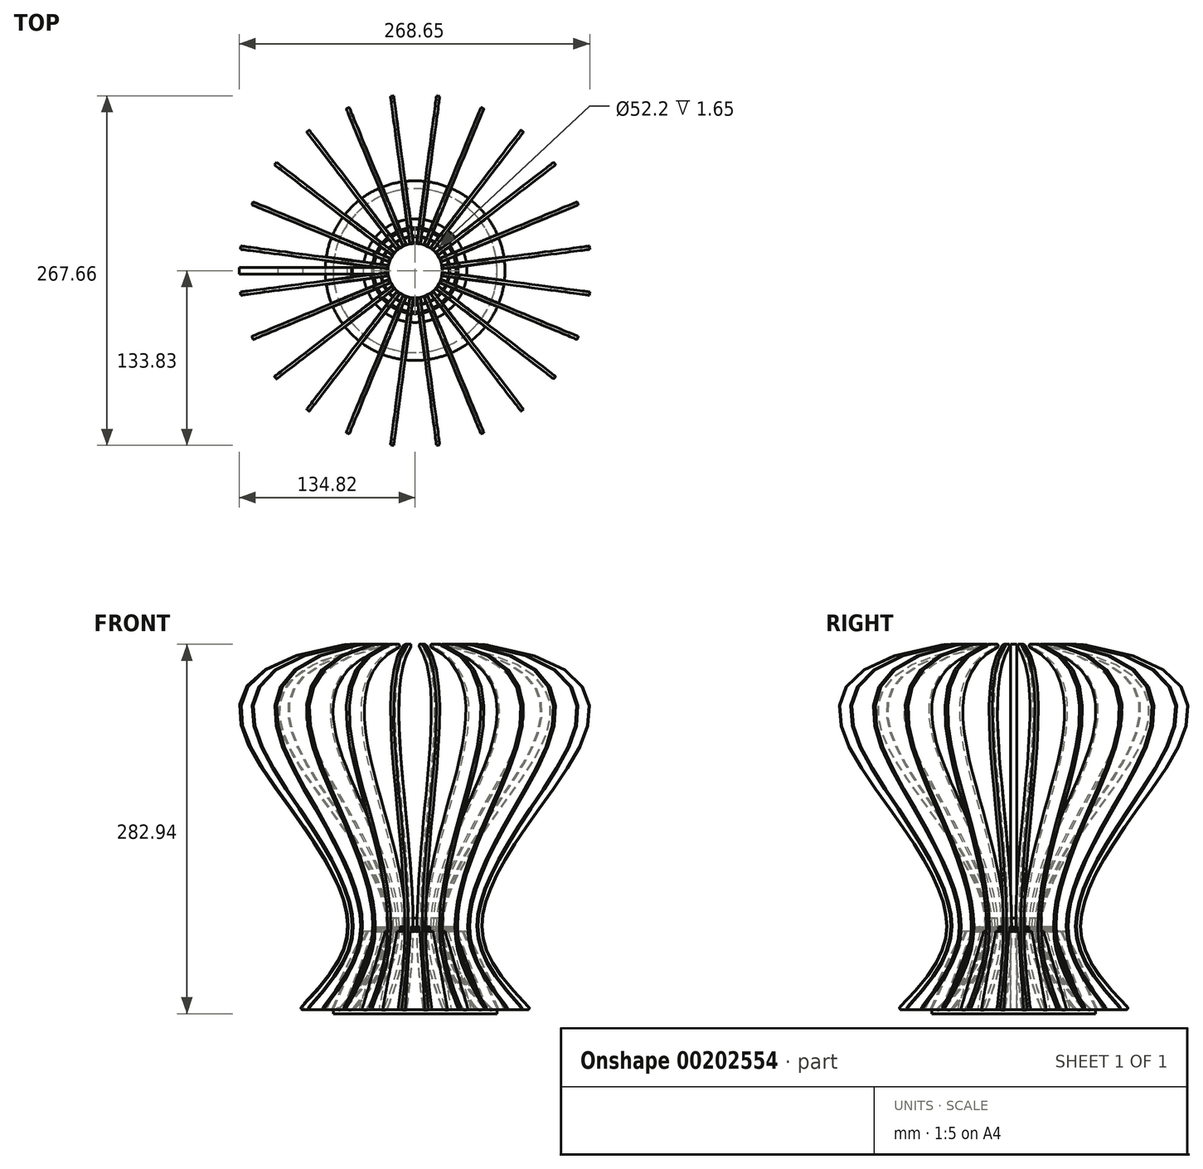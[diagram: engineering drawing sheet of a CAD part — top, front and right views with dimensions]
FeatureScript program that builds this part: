
annotation { "Feature Type Name" : "Feature", "Feature Type Description" : "" }
export const myFeature = defineFeature(function(context is Context, id is Id, definition is map)
    precondition{}
    {
        {
            var Q0;
            Q0=qCreatedBy(makeId("Top.planeOp"),FACE);
            var sketch = newSketch(context, id + "F0", { "sketchPlane" : qUnion([Q0])});
            skCircle(sketch, "E0", {"center": v(0, 0) * mm, "radius": 32.75 * mm});
            skCircle(sketch, "E1", {"center": v(0, 0) * mm, "radius": 26.1 * mm});
            skSolve(sketch);
        }
        {
            var Q0;
            Q0=qSketchRegion(id+"F0",true);
            extrude(context, id + "F1", {"entities" : qUnion([Q0]), "depth" : 1.65 * mm});
        }
        {
            var Q0;
            Q0=makeQuery(id+"F1.opExtrude","CAP_FACE",FACE,{"disambiguationData":[OSD([sQuery(id+"F0.wireOp",EDGE,"E0"),sQuery(id+"F0.wireOp",EDGE,"E1")])],"isStart":false});
            var sketch = newSketch(context, id + "F2", { "sketchPlane" : qUnion([Q0])});
            skLineSegment(sketch, "E2.bottom", {"start": v(2.5, -26.5) * mm, "end": v(-2.5, -26.5) * mm});
            skLineSegment(sketch, "E2.top", {"start": v(2.5, -31.5) * mm, "end": v(-2.5, -31.5) * mm});
            skLineSegment(sketch, "E2.left", {"start": v(2.5, -26.5) * mm, "end": v(2.5, -31.5) * mm});
            skLineSegment(sketch, "E2.right", {"start": v(-2.5, -26.5) * mm, "end": v(-2.5, -31.5) * mm});
            skPoint(sketch, "E2.middle", {"position": v(0, -29) * mm});
            skSolve(sketch);
        }
        {
            var Q0;
            Q0=makeQuery(id+"F2.imprint","IMPRINT",FACE,{"disambiguationData":[TD([[makeQuery(id+"F2.imprint","IMPRINT",EDGE,{"derivedFrom":sQuery(id+"F2.wireOp",EDGE,"E2.bottom")}),1.0]])]});
            extrude(context, id + "F3", {"entities" : qUnion([Q0]), "depth" : 1.62 * mm});
        }
        {
            var Q0;
            Q0=makeQuery(id+"F3.opExtrude","SWEPT_BODY",BODY,{"disambiguationData":[OSD([sQuery(id+"F2.wireOp",EDGE,"E2.bottom"),sQuery(id+"F2.wireOp",EDGE,"E2.top"),sQuery(id+"F2.wireOp",EDGE,"E2.left"),sQuery(id+"F2.wireOp",EDGE,"E2.right")])]});
            var Q1;
            Q1=makeQuery(id+"F1.opExtrude","CAP_EDGE",EDGE,{"disambiguationData":[OSD([sQuery(id+"F0.wireOp",EDGE,"E0")])],"isStart":false});
            circularPattern(context, id + "F4", {"entities" : qUnion([Q0]), "axis" : qUnion([Q1]), "angle" : 360 * degree, "instanceCount" : 24, "equalSpace" : true});
        }
        {
            var Q0;
            Q0=qCreatedBy(makeId("Front.planeOp"),FACE);
            var sketch = newSketch(context, id + "F5", { "sketchPlane" : qUnion([Q0])});
            skFitSpline(sketch, "E3", {"points": [v(-52, 220) * mm, v(-100, 100) * mm, v(-52, 10) * mm, v(-90, -60) * mm], "startDerivative": vector(-1003.67, -146.83) * mm, "endDerivative": vector(-314.48, -306.5) * mm});
            skLineSegment(sketch, "E4", {"start": v(-9.97, -59.99) * mm, "end": v(-9.97, -0.01) * mm, "construction": true});
            skLineSegment(sketch, "E5", {"start": v(-9.97, -0.01) * mm, "end": v(-33, -0.01) * mm});
            skLineSegment(sketch, "E6", {"start": v(-33, -0.01) * mm, "end": v(-33, 3.46) * mm});
            skLineSegment(sketch, "E7", {"start": v(-33, 3.46) * mm, "end": v(0, 3.46) * mm});
            skLineSegment(sketch, "E8", {"start": v(0, 3.46) * mm, "end": v(0, 369.62) * mm, "construction": true});
            skLineSegment(sketch, "E9", {"start": v(-22, 3.46) * mm, "end": v(-22, 220) * mm, "construction": true});
            skFitSpline(sketch, "E10", {"points": [v(-60, -60) * mm, v(-22, 10) * mm, v(-70, 100) * mm, v(-22, 220) * mm], "startDerivative": vector(314.48, 306.5) * mm, "endDerivative": vector(1003.67, 146.83) * mm});
            skLineSegment(sketch, "E11", {"start": v(-90, -60) * mm, "end": v(-60, -60) * mm});
            skLineSegment(sketch, "E12", {"start": v(-59.22, -30) * mm, "end": v(-29.22, -30) * mm, "construction": true});
            skLineSegment(sketch, "E13", {"start": v(-52, 10) * mm, "end": v(-22, 10) * mm, "construction": true});
            skLineSegment(sketch, "E14", {"start": v(-52, 220) * mm, "end": v(-22, 220) * mm});
            skLineSegment(sketch, "E15", {"start": v(-177.14, 201.7) * mm, "end": v(-147.14, 201.7) * mm, "construction": true});
            skLineSegment(sketch, "E16", {"start": v(-100, 100) * mm, "end": v(-70, 100) * mm, "construction": true});
            skPoint(sketch, "E17", {"position": v(-9.97, -30) * mm});
            skSolve(sketch);
        }
        {
            var Q0;
            Q0=makeQuery(id+"F5.imprint","IMPRINT",FACE,{"disambiguationData":[TD([[makeQuery(id+"F5.imprint","IMPRINT",EDGE,{"derivedFrom":sQuery(id+"F5.wireOp",EDGE,"E3")}),1.0]])]});
            extrude(context, id + "F6", {"entities" : qUnion([Q0]), "endBound" : BoundingType.SYMMETRIC, "depth" : 5 * mm});
        }
        {
            var Q0;
            Q0=makeQuery(id+"F6.opExtrude","SWEPT_EDGE",EDGE,{"disambiguationData":[OSD([sQuery(id+"F5.wireOp",EDGE,"E3"),sQuery(id+"F5.wireOp",EDGE,"E14")])]});
            fillet(context, id + "F7", {"entities" : qUnion([Q0]), "radius" : 46.48 * mm, "tangentPropagation" : true, "allowEdgeOverflow" : false});
        }
        {
            var Q0;
            Q0=makeQuery(id+"F6.opExtrude","SWEPT_EDGE",EDGE,{"disambiguationData":[OSD([sQuery(id+"F5.wireOp",EDGE,"E10"),sQuery(id+"F5.wireOp",EDGE,"E14")])]});
            fillet(context, id + "F8", {"entities" : qUnion([Q0]), "radius" : 3.7 * mm, "tangentPropagation" : true, "allowEdgeOverflow" : false});
        }
        {
            var Q0;
            Q0=makeQuery(id+"F6.opExtrude","SWEPT_EDGE",EDGE,{"disambiguationData":[OSD([sQuery(id+"F5.wireOp",EDGE,"E3"),sQuery(id+"F5.wireOp",EDGE,"E11")])]});
            fillet(context, id + "F9", {"entities" : qUnion([Q0]), "radius" : 2.86 * mm, "tangentPropagation" : true, "allowEdgeOverflow" : false});
        }
        {
            var Q0;
            Q0=makeQuery(id+"F6.opExtrude","SWEPT_EDGE",EDGE,{"disambiguationData":[OSD([sQuery(id+"F5.wireOp",EDGE,"E10"),sQuery(id+"F5.wireOp",EDGE,"E11")])]});
            fillet(context, id + "F10", {"entities" : qUnion([Q0]), "radius" : 13.3 * mm, "tangentPropagation" : true, "allowEdgeOverflow" : false});
        }
        {
            var Q0;
            Q0=makeQuery(id+"F5.imprint","IMPRINT",FACE,{"disambiguationData":[TD([[makeQuery(id+"F5.imprint","IMPRINT",EDGE,{"derivedFrom":sQuery(id+"F5.wireOp",EDGE,"E3")}),1.0]])]});
            extrude(context, id + "F11", {"entities" : qUnion([Q0]), "endBound" : BoundingType.SYMMETRIC, "depth" : 2.5 * mm});
        }
        {
            var Q0;
            Q0=makeQuery(id+"F11.opExtrude","SWEPT_EDGE",EDGE,{"disambiguationData":[OSD([sQuery(id+"F5.wireOp",EDGE,"E3"),sQuery(id+"F5.wireOp",EDGE,"E14")])]});
            fillet(context, id + "F12", {"entities" : qUnion([Q0]), "radius" : 59.56 * mm, "tangentPropagation" : true, "allowEdgeOverflow" : false});
        }
        {
            var Q0;
            Q0=makeQuery(id+"F11.opExtrude","SWEPT_EDGE",EDGE,{"disambiguationData":[OSD([sQuery(id+"F5.wireOp",EDGE,"E10"),sQuery(id+"F5.wireOp",EDGE,"E14")])]});
            fillet(context, id + "F13", {"entities" : qUnion([Q0]), "radius" : 1.1 * mm, "tangentPropagation" : true, "allowEdgeOverflow" : false});
        }
        {
            var Q0;
            Q0=makeQuery(id+"F11.opExtrude","SWEPT_EDGE",EDGE,{"disambiguationData":[OSD([sQuery(id+"F5.wireOp",EDGE,"E3"),sQuery(id+"F5.wireOp",EDGE,"E11")])]});
            fillet(context, id + "F14", {"entities" : qUnion([Q0]), "radius" : 1.37 * mm, "tangentPropagation" : true, "allowEdgeOverflow" : false});
        }
        {
            var Q0;
            Q0=makeQuery(id+"F11.opExtrude","SWEPT_EDGE",EDGE,{"disambiguationData":[OSD([sQuery(id+"F5.wireOp",EDGE,"E10"),sQuery(id+"F5.wireOp",EDGE,"E11")])]});
            fillet(context, id + "F15", {"entities" : qUnion([Q0]), "radius" : 6.04 * mm, "tangentPropagation" : true, "allowEdgeOverflow" : false});
        }
        {
            var Q0;
            Q0=makeQuery(id+"F11.opExtrude","SWEPT_BODY",BODY,{"disambiguationData":[OSD([sQuery(id+"F5.wireOp",EDGE,"E3"),sQuery(id+"F5.wireOp",EDGE,"E5"),sQuery(id+"F5.wireOp",EDGE,"E6"),sQuery(id+"F5.wireOp",EDGE,"E7"),sQuery(id+"F5.wireOp",EDGE,"E10"),sQuery(id+"F5.wireOp",EDGE,"E11"),sQuery(id+"F5.wireOp",EDGE,"E14")])]});
            var Q1;
            Q1=sQuery(id+"F5.wireOp",EDGE,"E8");
            transform(context, id + "F16", {"entities" : qUnion([Q0]), "transformType" : TransformType.ROTATION, "transformAxis" : qUnion([Q1]), "angle" : 7.5 * degree, "makeCopy" : false});
        }
        {
            var Q0;
            Q0=makeQuery(id+"F11.opExtrude","SWEPT_BODY",BODY,{"disambiguationData":[OSD([sQuery(id+"F5.wireOp",EDGE,"E3"),sQuery(id+"F5.wireOp",EDGE,"E5"),sQuery(id+"F5.wireOp",EDGE,"E6"),sQuery(id+"F5.wireOp",EDGE,"E7"),sQuery(id+"F5.wireOp",EDGE,"E10"),sQuery(id+"F5.wireOp",EDGE,"E11"),sQuery(id+"F5.wireOp",EDGE,"E14")])]});
            var Q1;
            Q1=sQuery(id+"F5.wireOp",EDGE,"E8");
            circularPattern(context, id + "F17", {"entities" : qUnion([Q0]), "axis" : qUnion([Q1]), "angle" : 360 * degree, "instanceCount" : 24, "equalSpace" : true});
        }
        {
            var Q0;
            Q0=qCreatedBy(makeId("Front.planeOp"),FACE);
            var sketch = newSketch(context, id + "F18", { "sketchPlane" : qUnion([Q0])});
            skLineSegment(sketch, "E18", {"start": v(0, -59.93) * mm, "end": v(-68.82, -59.93) * mm});
            skLineSegment(sketch, "E19", {"start": v(-68.82, -59.93) * mm, "end": v(-39.68, 0) * mm});
            skLineSegment(sketch, "E20", {"start": v(-39.68, 0) * mm, "end": v(-20.78, 0) * mm});
            skLineSegment(sketch, "E21", {"start": v(-20.78, 0) * mm, "end": v(-20.78, 10.18) * mm});
            skLineSegment(sketch, "E22", {"start": v(-20.78, 10.18) * mm, "end": v(0, 10.18) * mm});
            skLineSegment(sketch, "E23", {"start": v(0, 10.18) * mm, "end": v(0, -59.93) * mm});
            skLineSegment(sketch, "E24", {"start": v(-62.79, -59.93) * mm, "end": v(-62.79, -62.94) * mm});
            skLineSegment(sketch, "E25", {"start": v(-62.79, -62.94) * mm, "end": v(0, -62.94) * mm});
            skLineSegment(sketch, "E26", {"start": v(0, -62.94) * mm, "end": v(0, -59.93) * mm});
            skSolve(sketch);
        }
        {
            var Q0;
            {var subQ0=sQuery(id+"F18.wireOp",EDGE,"E19");Q0=makeQuery(id+"F18.imprint","IMPRINT",FACE,{"disambiguationData":[TD([[makeQuery(id+"F18.imprint","IMPRINT",EDGE,{"derivedFrom":subQ0}),-1.0]])]});}
            var Q1;
            {var subQ2=sQuery(id+"F18.wireOp",EDGE,"E24");Q1=makeQuery(id+"F18.imprint","IMPRINT",FACE,{"disambiguationData":[TD([[makeQuery(id+"F18.imprint","IMPRINT",EDGE,{"derivedFrom":subQ2}),1.0]])]});}
            var Q2;
            Q2=sQuery(id+"F18.wireOp",EDGE,"E23");
            revolve(context, id + "F19", {"entities" : qUnion([Q0, Q1]), "axis" : qUnion([Q2]), "revolveType" : RevolveType.FULL});
        }
        {
            var Q0;
            Q0=makeQuery(id+"F17.opPattern","COPY",BODY,{"derivedFrom":makeQuery(id+"F11.opExtrude","SWEPT_BODY",BODY,{"disambiguationData":[OSD([sQuery(id+"F5.wireOp",EDGE,"E3"),sQuery(id+"F5.wireOp",EDGE,"E5"),sQuery(id+"F5.wireOp",EDGE,"E6"),sQuery(id+"F5.wireOp",EDGE,"E7"),sQuery(id+"F5.wireOp",EDGE,"E10"),sQuery(id+"F5.wireOp",EDGE,"E11"),sQuery(id+"F5.wireOp",EDGE,"E14")])]}),"instanceName":"3"});
            var Q1;
            Q1=makeQuery(id+"F17.opPattern","COPY",BODY,{"derivedFrom":makeQuery(id+"F11.opExtrude","SWEPT_BODY",BODY,{"disambiguationData":[OSD([sQuery(id+"F5.wireOp",EDGE,"E3"),sQuery(id+"F5.wireOp",EDGE,"E5"),sQuery(id+"F5.wireOp",EDGE,"E6"),sQuery(id+"F5.wireOp",EDGE,"E7"),sQuery(id+"F5.wireOp",EDGE,"E10"),sQuery(id+"F5.wireOp",EDGE,"E11"),sQuery(id+"F5.wireOp",EDGE,"E14")])]}),"instanceName":"4"});
            var Q2;
            Q2=makeQuery(id+"F17.opPattern","COPY",BODY,{"derivedFrom":makeQuery(id+"F11.opExtrude","SWEPT_BODY",BODY,{"disambiguationData":[OSD([sQuery(id+"F5.wireOp",EDGE,"E3"),sQuery(id+"F5.wireOp",EDGE,"E5"),sQuery(id+"F5.wireOp",EDGE,"E6"),sQuery(id+"F5.wireOp",EDGE,"E7"),sQuery(id+"F5.wireOp",EDGE,"E10"),sQuery(id+"F5.wireOp",EDGE,"E11"),sQuery(id+"F5.wireOp",EDGE,"E14")])]}),"instanceName":"5"});
            var Q3;
            Q3=makeQuery(id+"F17.opPattern","COPY",BODY,{"derivedFrom":makeQuery(id+"F11.opExtrude","SWEPT_BODY",BODY,{"disambiguationData":[OSD([sQuery(id+"F5.wireOp",EDGE,"E3"),sQuery(id+"F5.wireOp",EDGE,"E5"),sQuery(id+"F5.wireOp",EDGE,"E6"),sQuery(id+"F5.wireOp",EDGE,"E7"),sQuery(id+"F5.wireOp",EDGE,"E10"),sQuery(id+"F5.wireOp",EDGE,"E11"),sQuery(id+"F5.wireOp",EDGE,"E14")])]}),"instanceName":"6"});
            var Q4;
            Q4=makeQuery(id+"F17.opPattern","COPY",BODY,{"derivedFrom":makeQuery(id+"F11.opExtrude","SWEPT_BODY",BODY,{"disambiguationData":[OSD([sQuery(id+"F5.wireOp",EDGE,"E3"),sQuery(id+"F5.wireOp",EDGE,"E5"),sQuery(id+"F5.wireOp",EDGE,"E6"),sQuery(id+"F5.wireOp",EDGE,"E7"),sQuery(id+"F5.wireOp",EDGE,"E10"),sQuery(id+"F5.wireOp",EDGE,"E11"),sQuery(id+"F5.wireOp",EDGE,"E14")])]}),"instanceName":"7"});
            var Q5;
            Q5=makeQuery(id+"F17.opPattern","COPY",BODY,{"derivedFrom":makeQuery(id+"F11.opExtrude","SWEPT_BODY",BODY,{"disambiguationData":[OSD([sQuery(id+"F5.wireOp",EDGE,"E3"),sQuery(id+"F5.wireOp",EDGE,"E5"),sQuery(id+"F5.wireOp",EDGE,"E6"),sQuery(id+"F5.wireOp",EDGE,"E7"),sQuery(id+"F5.wireOp",EDGE,"E10"),sQuery(id+"F5.wireOp",EDGE,"E11"),sQuery(id+"F5.wireOp",EDGE,"E14")])]}),"instanceName":"8"});
            var Q6;
            Q6=makeQuery(id+"F17.opPattern","COPY",BODY,{"derivedFrom":makeQuery(id+"F11.opExtrude","SWEPT_BODY",BODY,{"disambiguationData":[OSD([sQuery(id+"F5.wireOp",EDGE,"E3"),sQuery(id+"F5.wireOp",EDGE,"E5"),sQuery(id+"F5.wireOp",EDGE,"E6"),sQuery(id+"F5.wireOp",EDGE,"E7"),sQuery(id+"F5.wireOp",EDGE,"E10"),sQuery(id+"F5.wireOp",EDGE,"E11"),sQuery(id+"F5.wireOp",EDGE,"E14")])]}),"instanceName":"9"});
            var Q7;
            Q7=makeQuery(id+"F17.opPattern","COPY",BODY,{"derivedFrom":makeQuery(id+"F11.opExtrude","SWEPT_BODY",BODY,{"disambiguationData":[OSD([sQuery(id+"F5.wireOp",EDGE,"E3"),sQuery(id+"F5.wireOp",EDGE,"E5"),sQuery(id+"F5.wireOp",EDGE,"E6"),sQuery(id+"F5.wireOp",EDGE,"E7"),sQuery(id+"F5.wireOp",EDGE,"E10"),sQuery(id+"F5.wireOp",EDGE,"E11"),sQuery(id+"F5.wireOp",EDGE,"E14")])]}),"instanceName":"10"});
            var Q8;
            Q8=makeQuery(id+"F17.opPattern","COPY",BODY,{"derivedFrom":makeQuery(id+"F11.opExtrude","SWEPT_BODY",BODY,{"disambiguationData":[OSD([sQuery(id+"F5.wireOp",EDGE,"E3"),sQuery(id+"F5.wireOp",EDGE,"E5"),sQuery(id+"F5.wireOp",EDGE,"E6"),sQuery(id+"F5.wireOp",EDGE,"E7"),sQuery(id+"F5.wireOp",EDGE,"E10"),sQuery(id+"F5.wireOp",EDGE,"E11"),sQuery(id+"F5.wireOp",EDGE,"E14")])]}),"instanceName":"11"});
            var Q9;
            Q9=makeQuery(id+"F17.opPattern","COPY",BODY,{"derivedFrom":makeQuery(id+"F11.opExtrude","SWEPT_BODY",BODY,{"disambiguationData":[OSD([sQuery(id+"F5.wireOp",EDGE,"E3"),sQuery(id+"F5.wireOp",EDGE,"E5"),sQuery(id+"F5.wireOp",EDGE,"E6"),sQuery(id+"F5.wireOp",EDGE,"E7"),sQuery(id+"F5.wireOp",EDGE,"E10"),sQuery(id+"F5.wireOp",EDGE,"E11"),sQuery(id+"F5.wireOp",EDGE,"E14")])]}),"instanceName":"12"});
            var Q10;
            Q10=makeQuery(id+"F17.opPattern","COPY",BODY,{"derivedFrom":makeQuery(id+"F11.opExtrude","SWEPT_BODY",BODY,{"disambiguationData":[OSD([sQuery(id+"F5.wireOp",EDGE,"E3"),sQuery(id+"F5.wireOp",EDGE,"E5"),sQuery(id+"F5.wireOp",EDGE,"E6"),sQuery(id+"F5.wireOp",EDGE,"E7"),sQuery(id+"F5.wireOp",EDGE,"E10"),sQuery(id+"F5.wireOp",EDGE,"E11"),sQuery(id+"F5.wireOp",EDGE,"E14")])]}),"instanceName":"13"});
            var Q11;
            Q11=makeQuery(id+"F17.opPattern","COPY",BODY,{"derivedFrom":makeQuery(id+"F11.opExtrude","SWEPT_BODY",BODY,{"disambiguationData":[OSD([sQuery(id+"F5.wireOp",EDGE,"E3"),sQuery(id+"F5.wireOp",EDGE,"E5"),sQuery(id+"F5.wireOp",EDGE,"E6"),sQuery(id+"F5.wireOp",EDGE,"E7"),sQuery(id+"F5.wireOp",EDGE,"E10"),sQuery(id+"F5.wireOp",EDGE,"E11"),sQuery(id+"F5.wireOp",EDGE,"E14")])]}),"instanceName":"14"});
            var Q12;
            Q12=makeQuery(id+"F17.opPattern","COPY",BODY,{"derivedFrom":makeQuery(id+"F11.opExtrude","SWEPT_BODY",BODY,{"disambiguationData":[OSD([sQuery(id+"F5.wireOp",EDGE,"E3"),sQuery(id+"F5.wireOp",EDGE,"E5"),sQuery(id+"F5.wireOp",EDGE,"E6"),sQuery(id+"F5.wireOp",EDGE,"E7"),sQuery(id+"F5.wireOp",EDGE,"E10"),sQuery(id+"F5.wireOp",EDGE,"E11"),sQuery(id+"F5.wireOp",EDGE,"E14")])]}),"instanceName":"15"});
            var Q13;
            Q13=makeQuery(id+"F17.opPattern","COPY",BODY,{"derivedFrom":makeQuery(id+"F11.opExtrude","SWEPT_BODY",BODY,{"disambiguationData":[OSD([sQuery(id+"F5.wireOp",EDGE,"E3"),sQuery(id+"F5.wireOp",EDGE,"E5"),sQuery(id+"F5.wireOp",EDGE,"E6"),sQuery(id+"F5.wireOp",EDGE,"E7"),sQuery(id+"F5.wireOp",EDGE,"E10"),sQuery(id+"F5.wireOp",EDGE,"E11"),sQuery(id+"F5.wireOp",EDGE,"E14")])]}),"instanceName":"16"});
            var Q14;
            Q14=makeQuery(id+"F17.opPattern","COPY",BODY,{"derivedFrom":makeQuery(id+"F11.opExtrude","SWEPT_BODY",BODY,{"disambiguationData":[OSD([sQuery(id+"F5.wireOp",EDGE,"E3"),sQuery(id+"F5.wireOp",EDGE,"E5"),sQuery(id+"F5.wireOp",EDGE,"E6"),sQuery(id+"F5.wireOp",EDGE,"E7"),sQuery(id+"F5.wireOp",EDGE,"E10"),sQuery(id+"F5.wireOp",EDGE,"E11"),sQuery(id+"F5.wireOp",EDGE,"E14")])]}),"instanceName":"17"});
            var Q15;
            Q15=makeQuery(id+"F17.opPattern","COPY",BODY,{"derivedFrom":makeQuery(id+"F11.opExtrude","SWEPT_BODY",BODY,{"disambiguationData":[OSD([sQuery(id+"F5.wireOp",EDGE,"E3"),sQuery(id+"F5.wireOp",EDGE,"E5"),sQuery(id+"F5.wireOp",EDGE,"E6"),sQuery(id+"F5.wireOp",EDGE,"E7"),sQuery(id+"F5.wireOp",EDGE,"E10"),sQuery(id+"F5.wireOp",EDGE,"E11"),sQuery(id+"F5.wireOp",EDGE,"E14")])]}),"instanceName":"18"});
            var Q16;
            Q16=makeQuery(id+"F17.opPattern","COPY",BODY,{"derivedFrom":makeQuery(id+"F11.opExtrude","SWEPT_BODY",BODY,{"disambiguationData":[OSD([sQuery(id+"F5.wireOp",EDGE,"E3"),sQuery(id+"F5.wireOp",EDGE,"E5"),sQuery(id+"F5.wireOp",EDGE,"E6"),sQuery(id+"F5.wireOp",EDGE,"E7"),sQuery(id+"F5.wireOp",EDGE,"E10"),sQuery(id+"F5.wireOp",EDGE,"E11"),sQuery(id+"F5.wireOp",EDGE,"E14")])]}),"instanceName":"20"});
            var Q17;
            Q17=makeQuery(id+"F17.opPattern","COPY",BODY,{"derivedFrom":makeQuery(id+"F11.opExtrude","SWEPT_BODY",BODY,{"disambiguationData":[OSD([sQuery(id+"F5.wireOp",EDGE,"E3"),sQuery(id+"F5.wireOp",EDGE,"E5"),sQuery(id+"F5.wireOp",EDGE,"E6"),sQuery(id+"F5.wireOp",EDGE,"E7"),sQuery(id+"F5.wireOp",EDGE,"E10"),sQuery(id+"F5.wireOp",EDGE,"E11"),sQuery(id+"F5.wireOp",EDGE,"E14")])]}),"instanceName":"21"});
            var Q18;
            Q18=makeQuery(id+"F17.opPattern","COPY",BODY,{"derivedFrom":makeQuery(id+"F11.opExtrude","SWEPT_BODY",BODY,{"disambiguationData":[OSD([sQuery(id+"F5.wireOp",EDGE,"E3"),sQuery(id+"F5.wireOp",EDGE,"E5"),sQuery(id+"F5.wireOp",EDGE,"E6"),sQuery(id+"F5.wireOp",EDGE,"E7"),sQuery(id+"F5.wireOp",EDGE,"E10"),sQuery(id+"F5.wireOp",EDGE,"E11"),sQuery(id+"F5.wireOp",EDGE,"E14")])]}),"instanceName":"22"});
            var Q19;
            Q19=makeQuery(id+"F17.opPattern","COPY",BODY,{"derivedFrom":makeQuery(id+"F11.opExtrude","SWEPT_BODY",BODY,{"disambiguationData":[OSD([sQuery(id+"F5.wireOp",EDGE,"E3"),sQuery(id+"F5.wireOp",EDGE,"E5"),sQuery(id+"F5.wireOp",EDGE,"E6"),sQuery(id+"F5.wireOp",EDGE,"E7"),sQuery(id+"F5.wireOp",EDGE,"E10"),sQuery(id+"F5.wireOp",EDGE,"E11"),sQuery(id+"F5.wireOp",EDGE,"E14")])]}),"instanceName":"1"});
            var Q20;
            Q20=makeQuery(id+"F11.opExtrude","SWEPT_BODY",BODY,{"disambiguationData":[OSD([sQuery(id+"F5.wireOp",EDGE,"E3"),sQuery(id+"F5.wireOp",EDGE,"E5"),sQuery(id+"F5.wireOp",EDGE,"E6"),sQuery(id+"F5.wireOp",EDGE,"E7"),sQuery(id+"F5.wireOp",EDGE,"E10"),sQuery(id+"F5.wireOp",EDGE,"E11"),sQuery(id+"F5.wireOp",EDGE,"E14")])]});
            var Q21;
            Q21=makeQuery(id+"F17.opPattern","COPY",BODY,{"derivedFrom":makeQuery(id+"F11.opExtrude","SWEPT_BODY",BODY,{"disambiguationData":[OSD([sQuery(id+"F5.wireOp",EDGE,"E3"),sQuery(id+"F5.wireOp",EDGE,"E5"),sQuery(id+"F5.wireOp",EDGE,"E6"),sQuery(id+"F5.wireOp",EDGE,"E7"),sQuery(id+"F5.wireOp",EDGE,"E10"),sQuery(id+"F5.wireOp",EDGE,"E11"),sQuery(id+"F5.wireOp",EDGE,"E14")])]}),"instanceName":"2"});
            var Q22;
            Q22=makeQuery(id+"F17.opPattern","COPY",BODY,{"derivedFrom":makeQuery(id+"F11.opExtrude","SWEPT_BODY",BODY,{"disambiguationData":[OSD([sQuery(id+"F5.wireOp",EDGE,"E3"),sQuery(id+"F5.wireOp",EDGE,"E5"),sQuery(id+"F5.wireOp",EDGE,"E6"),sQuery(id+"F5.wireOp",EDGE,"E7"),sQuery(id+"F5.wireOp",EDGE,"E10"),sQuery(id+"F5.wireOp",EDGE,"E11"),sQuery(id+"F5.wireOp",EDGE,"E14")])]}),"instanceName":"19"});
            var Q23;
            Q23=makeQuery(id+"F17.opPattern","COPY",BODY,{"derivedFrom":makeQuery(id+"F11.opExtrude","SWEPT_BODY",BODY,{"disambiguationData":[OSD([sQuery(id+"F5.wireOp",EDGE,"E3"),sQuery(id+"F5.wireOp",EDGE,"E5"),sQuery(id+"F5.wireOp",EDGE,"E6"),sQuery(id+"F5.wireOp",EDGE,"E7"),sQuery(id+"F5.wireOp",EDGE,"E10"),sQuery(id+"F5.wireOp",EDGE,"E11"),sQuery(id+"F5.wireOp",EDGE,"E14")])]}),"instanceName":"23"});
            var Q24;
            Q24=makeQuery(id+"F1.opExtrude","SWEPT_BODY",BODY,{"disambiguationData":[OSD([sQuery(id+"F0.wireOp",EDGE,"E0"),sQuery(id+"F0.wireOp",EDGE,"E1")])]});
            var Q25;
            Q25=makeQuery(id+"F19.opRevolve","SWEPT_BODY",BODY,{"disambiguationData":[OSD([sQuery(id+"F18.wireOp",EDGE,"E18"),sQuery(id+"F18.wireOp",EDGE,"E19"),sQuery(id+"F18.wireOp",EDGE,"E20"),sQuery(id+"F18.wireOp",EDGE,"E21"),sQuery(id+"F18.wireOp",EDGE,"E22"),sQuery(id+"F18.wireOp",EDGE,"E23"),sQuery(id+"F18.wireOp",EDGE,"E24"),sQuery(id+"F18.wireOp",EDGE,"E25"),sQuery(id+"F18.wireOp",EDGE,"E26")])]});
            booleanBodies(context, id + "F20", {"operationType" : BooleanOperationType.SUBTRACTION, "tools" : qUnion([Q0, Q1, Q2, Q3, Q4, Q5, Q6, Q7, Q8, Q9, Q10, Q11, Q12, Q13, Q14, Q15, Q16, Q17, Q18, Q19, Q20, Q21, Q22, Q23, Q24]), "targets" : qUnion([Q25]), "offset" : true, "offsetAll" : true, "offsetDistance" : .25 * mm, "keepTools" : true});
        }
    });
